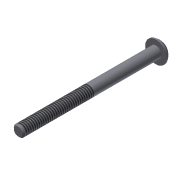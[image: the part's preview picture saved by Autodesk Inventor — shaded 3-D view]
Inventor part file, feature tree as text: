
AUTODESK INVENTOR PART (.ipt)
format: ipt  version: 2013 (Build 170138000, 138)  size: 120,832 bytes
history: native  units: in
note: dims shown in document units (in); Inventor stores cm internally (conversion verified against a paired STEP export)
features: sketch x3, extrude x2, revolve x1, chamfer x1, thread x1
ambient origin geometry x8: Origin, YZ Plane, XZ Plane, XY Plane, X Axis, Y Axis, Z Axis, Center Point
bodies: Solid1 (feature_tree)
feature tree (8):
  extrude  "Extrusion1"  Depth=2.0in TaperAngle=0.0deg
  revolve  "Revolution1"  [1 undecoded]
  extrude  "Extrusion2"  Depth=0.0938in
  chamfer  "Chamfer1"  Distance=0.0625in
  thread  "Thread1"  [1 undecoded]
  sketch  "Sketch1"  dims[d0=0.164in d1=2.0in d2=0.0in]
  sketch  "Sketch2"  dims[d3=0.087in d6=0.08in]
  sketch  "Sketch3"  dims[d7=90.0deg d8=0.0938in d9=0.0625in d10=0.0in d13=0.02in d14=0.125in d15=45.0deg d16=1.0in d17=0.0in d19=0.156in]
note: 2 required parameter values undecoded (feature->parameter linkage not recoverable at this tier; creation-order binding heuristic only, values carry confidence <= 0.55)